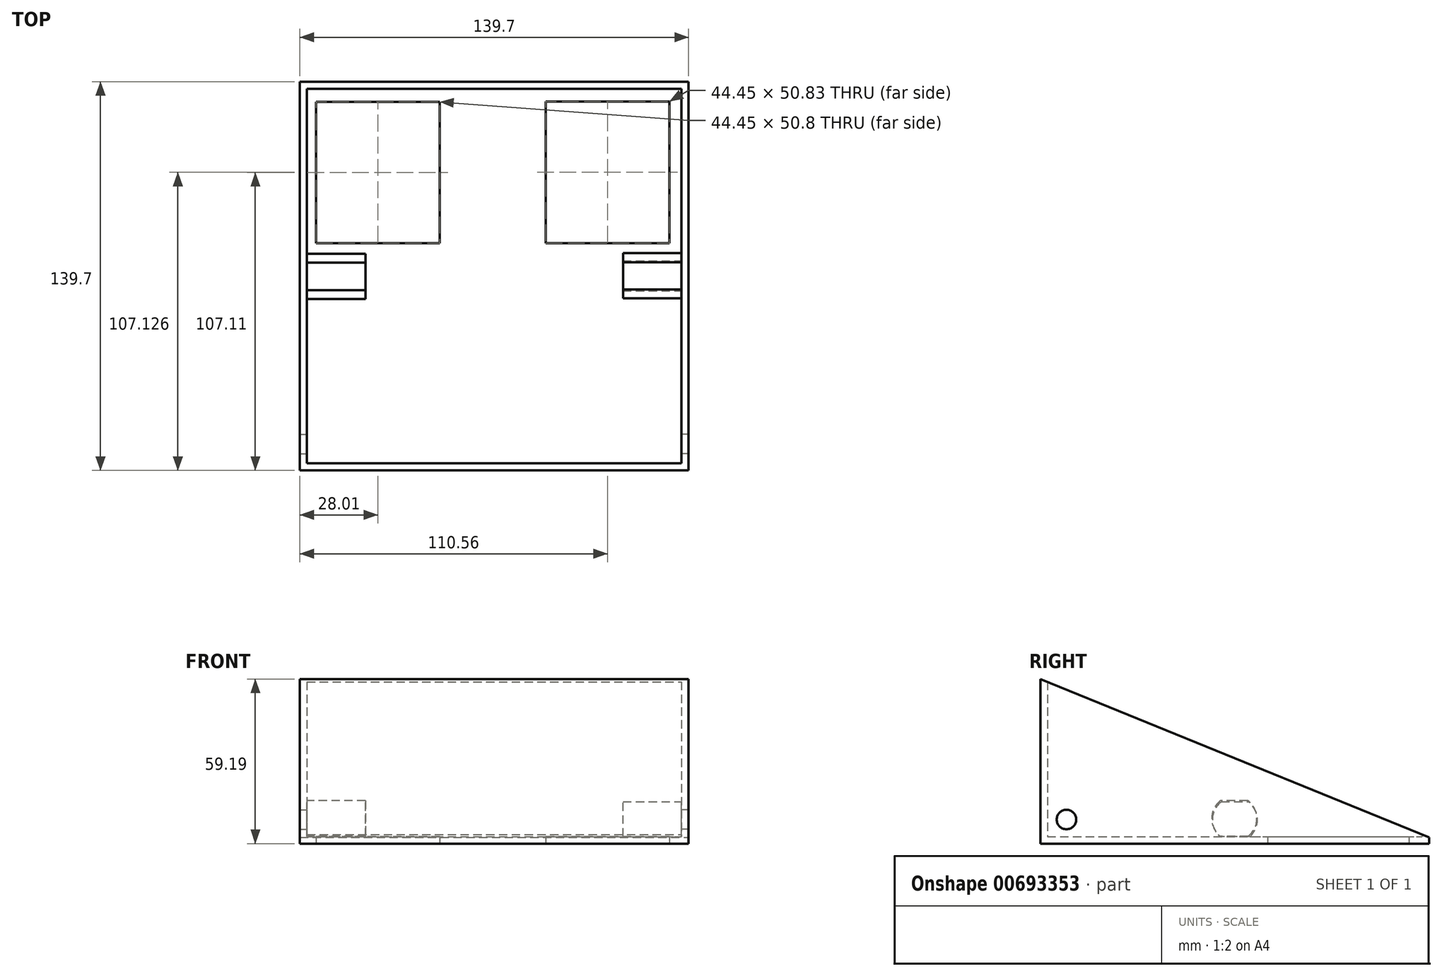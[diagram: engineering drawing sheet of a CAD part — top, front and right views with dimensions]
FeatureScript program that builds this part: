
annotation { "Feature Type Name" : "Feature", "Feature Type Description" : "" }
export const myFeature = defineFeature(function(context is Context, id is Id, definition is map)
    precondition{}
    {
        {
            var Q0;
            Q0=qCreatedBy(makeId("Front.planeOp"),FACE);
            var sketch = newSketch(context, id + "F0", { "sketchPlane" : qUnion([Q0])});
            skLineSegment(sketch, "E0.bottom", {"start": v(-62.53, 207.24) * mm, "end": v(77.17, 207.24) * mm});
            skLineSegment(sketch, "E0.top", {"start": v(-62.53, 67.54) * mm, "end": v(77.17, 67.54) * mm});
            skLineSegment(sketch, "E0.left", {"start": v(-62.53, 207.24) * mm, "end": v(-62.53, 67.54) * mm});
            skLineSegment(sketch, "E0.right", {"start": v(77.17, 207.24) * mm, "end": v(77.17, 67.54) * mm});
            skSolve(sketch);
        }
        {
            var Q0;
            Q0=qCreatedBy(makeId("Right.planeOp"),FACE);
            var sketch = newSketch(context, id + "F1", { "sketchPlane" : qUnion([Q0])});
            skCircle(sketch, "E1", {"center": v(-60.44, 76.2) * mm, "radius": 3.5 * mm});
            skSolve(sketch);
        }
        {
            var Q0;
            Q0 = qSketchRegion(id + "F0", true);
            extrude(context, id + "F2", {"entities" : qUnion([Q0]), "endBound" : BoundingType.SYMMETRIC, "depth" : 139.7 * mm, "offsetDistance" : 25.4 * mm});
        }
        {
            var Q0;
            Q0=qCreatedBy(makeId("Top.planeOp"),FACE);
            var sketch = newSketch(context, id + "F3", { "sketchPlane" : qUnion([Q0])});
            skLineSegment(sketch, "E2.bottom", {"start": v(-56.74, 62.66) * mm, "end": v(-12.3, 62.66) * mm});
            skLineSegment(sketch, "E2.top", {"start": v(-56.74, 62.66) * mm, "end": v(-12.3, 62.66) * mm});
            skLineSegment(sketch, "E2.left", {"start": v(-56.74, 62.66) * mm, "end": v(-56.74, 62.66) * mm});
            skLineSegment(sketch, "E2.right", {"start": v(-12.3, 62.66) * mm, "end": v(-12.3, 62.66) * mm});
            skLineSegment(sketch, "E3.top", {"start": v(-56.74, 11.86) * mm, "end": v(-12.3, 11.86) * mm});
            skLineSegment(sketch, "E3.left", {"start": v(-56.74, 62.66) * mm, "end": v(-56.74, 11.86) * mm});
            skLineSegment(sketch, "E3.right", {"start": v(-12.3, 62.66) * mm, "end": v(-12.3, 11.86) * mm});
            skLineSegment(sketch, "E4.bottom", {"start": v(25.8, 62.7) * mm, "end": v(70.26, 62.7) * mm});
            skLineSegment(sketch, "E4.top", {"start": v(25.8, 11.86) * mm, "end": v(70.26, 11.86) * mm});
            skLineSegment(sketch, "E4.left", {"start": v(25.8, 62.7) * mm, "end": v(25.8, 11.86) * mm});
            skLineSegment(sketch, "E4.right", {"start": v(70.26, 62.7) * mm, "end": v(70.26, 11.86) * mm});
            skSolve(sketch);
        }
        {
            var Q0;
            Q0 = qSketchRegion(id + "F3", true);
            extrude(context, id + "F4", {"entities" : qUnion([Q0]), "endBound" : BoundingType.SYMMETRIC, "depth" : 203.2 * mm, "offsetDistance" : 25.4 * mm});
        }
        {
            var Q0;
            Q0=qCreatedBy(makeId("Right.planeOp"),FACE);
            var sketch = newSketch(context, id + "F5", { "sketchPlane" : qUnion([Q0])});
            skLineSegment(sketch, "E5.bottom", {"start": v(134.32, 208.08) * mm, "end": v(-53.85, 284.79) * mm});
            skLineSegment(sketch, "E5.top", {"start": v(76.79, 66.96) * mm, "end": v(-111.38, 143.66) * mm});
            skLineSegment(sketch, "E5.left", {"start": v(134.32, 208.08) * mm, "end": v(76.79, 66.96) * mm});
            skLineSegment(sketch, "E5.right", {"start": v(-53.85, 284.79) * mm, "end": v(-111.38, 143.66) * mm});
            skSolve(sketch);
        }
        {
            var Q0;
            Q0 = qSketchRegion(id + "F5", true);
            extrude(context, id + "F6", {"entities" : qUnion([Q0]), "endBound" : BoundingType.SYMMETRIC, "depth" : 203.2 * mm, "offsetDistance" : 25.4 * mm});
        }
        {
            var Q0;
            Q0=makeQuery(id+"F6.opExtrude","SWEPT_BODY",BODY,{"disambiguationData":[OSD([sQuery(id+"F5.wireOp",EDGE,"E5.bottom"),sQuery(id+"F5.wireOp",EDGE,"E5.top"),sQuery(id+"F5.wireOp",EDGE,"E5.left"),sQuery(id+"F5.wireOp",EDGE,"E5.right")])]});
            var Q1;
            Q1=makeQuery(id+"F2.opExtrude","SWEPT_BODY",BODY,{"disambiguationData":[OSD([sQuery(id+"F0.wireOp",EDGE,"E0.bottom"),sQuery(id+"F0.wireOp",EDGE,"E0.top"),sQuery(id+"F0.wireOp",EDGE,"E0.left"),sQuery(id+"F0.wireOp",EDGE,"E0.right")])]});
            booleanBodies(context, id + "F7", {"operationType" : BooleanOperationType.SUBTRACTION, "tools" : qUnion([Q0]), "targets" : qUnion([Q1])});
        }
        {
            var Q0;
            Q0=makeQuery(id+"F7.opBoolean","COPY",FACE,{"derivedFrom":makeQuery(id+"F6.opExtrude","SWEPT_FACE",FACE,{"disambiguationData":[OSD([sQuery(id+"F5.wireOp",EDGE,"E5.top")])]})});
            shell(context, id + "F8", {"entities" : qUnion([Q0]), "thickness" : 2.54 * mm});
        }
        {
            var Q0;
            Q0=makeQuery(id+"F4.opExtrude","SWEPT_BODY",BODY,{"disambiguationData":[OSD([sQuery(id+"F3.wireOp",EDGE,"E4.bottom"),sQuery(id+"F3.wireOp",EDGE,"E4.top"),sQuery(id+"F3.wireOp",EDGE,"E4.left"),sQuery(id+"F3.wireOp",EDGE,"E4.right")])]});
            var Q1;
            Q1=makeQuery(id+"F4.opExtrude","SWEPT_BODY",BODY,{"disambiguationData":[OSD([sQuery(id+"F3.wireOp",EDGE,"E2.bottom"),sQuery(id+"F3.wireOp",EDGE,"E3.top"),sQuery(id+"F3.wireOp",EDGE,"E3.left"),sQuery(id+"F3.wireOp",EDGE,"E3.right")])]});
            var Q2;
            Q2=makeQuery(id+"F2.opExtrude","SWEPT_BODY",BODY,{"disambiguationData":[OSD([sQuery(id+"F0.wireOp",EDGE,"E0.bottom"),sQuery(id+"F0.wireOp",EDGE,"E0.top"),sQuery(id+"F0.wireOp",EDGE,"E0.left"),sQuery(id+"F0.wireOp",EDGE,"E0.right")])]});
            booleanBodies(context, id + "F9", {"operationType" : BooleanOperationType.SUBTRACTION, "tools" : qUnion([Q0, Q1]), "targets" : qUnion([Q2])});
        }
        {
            var Q0;
            Q0=sQuery(id+"F1.wireOp",VERTEX,"E1.center");
            var Q1;
            Q1=makeQuery(id+"F2.opExtrude","SWEPT_BODY",BODY,{"disambiguationData":[OSD([sQuery(id+"F0.wireOp",EDGE,"E0.bottom"),sQuery(id+"F0.wireOp",EDGE,"E0.top"),sQuery(id+"F0.wireOp",EDGE,"E0.left"),sQuery(id+"F0.wireOp",EDGE,"E0.right")])]});
            hole(context, id + "F10", {"style" : HoleStyle.SIMPLE, "endStyle" : HoleEndStyle.THROUGH, "holeDiameter" : 7 * mm, "majorDiameter" : 6.35 * mm, "isTappedThrough" : true, "tappedDepth" : 12.7 * mm, "tapClearance" : 3, "locations" : qUnion([Q0]), "scope" : qUnion([Q1])});
        }
        {
            var Q0;
            Q0=sQuery(id+"F1.wireOp",VERTEX,"E1.center");
            var Q1;
            Q1=makeQuery(id+"F2.opExtrude","SWEPT_BODY",BODY,{"disambiguationData":[OSD([sQuery(id+"F0.wireOp",EDGE,"E0.bottom"),sQuery(id+"F0.wireOp",EDGE,"E0.top"),sQuery(id+"F0.wireOp",EDGE,"E0.left"),sQuery(id+"F0.wireOp",EDGE,"E0.right")])]});
            hole(context, id + "F11", {"style" : HoleStyle.SIMPLE, "endStyle" : HoleEndStyle.THROUGH, "oppositeDirection" : true, "holeDiameter" : 7 * mm, "majorDiameter" : 6.35 * mm, "isTappedThrough" : true, "tappedDepth" : 12.7 * mm, "tapClearance" : 3, "locations" : qUnion([Q0]), "scope" : qUnion([Q1])});
        }
        {
            var Q0;
            Q0=makeQuery(id+"F8.opShell","OFFSET_FACE",FACE,{"disambiguationData":[OSD([sQuery(id+"F0.wireOp",EDGE,"E0.right")])]});
            var sketch = newSketch(context, id + "F12", { "sketchPlane" : qUnion([Q0])});
            skArc(sketch, "E6", {"start": v(-5, 82.55) * mm, "mid": v(-8.2, 76.1) * mm, "end": v(-5, 69.65) * mm});
            skArc(sketch, "E7.trimOffspring", {"start": v(4.83, 69.68) * mm, "mid": v(8, 76.12) * mm, "end": v(4.8, 82.55) * mm});
            skLineSegment(sketch, "E8.trimOffspring", {"start": v(4.83, 69.68) * mm, "end": v(-5, 69.65) * mm});
            skLineSegment(sketch, "E9.trimOffspring", {"start": v(4.8, 82.55) * mm, "end": v(-5, 82.55) * mm});
            skSolve(sketch);
        }
        {
            var Q0;
            Q0 = qSketchRegion(id + "F12", true);
            extrude(context, id + "F13", {"entities" : qUnion([Q0]), "operationType" : NewBodyOperationType.ADD, "depth" : 21 * mm, "offsetDistance" : 25.4 * mm});
        }
        {
            var Q0;
            Q0=makeQuery(id+"F8.opShell","OFFSET_FACE",FACE,{"disambiguationData":[OSD([sQuery(id+"F0.wireOp",EDGE,"E0.left")])]});
            var sketch = newSketch(context, id + "F14", { "sketchPlane" : qUnion([Q0])});
            skArc(sketch, "E10", {"start": v(-5.03, 83) * mm, "mid": v(-8.23, 76.55) * mm, "end": v(-5.03, 70.1) * mm});
            skArc(sketch, "E11.trimOffspring", {"start": v(4.8, 70.12) * mm, "mid": v(7.97, 76.56) * mm, "end": v(4.77, 83) * mm});
            skLineSegment(sketch, "E12.trimOffspring", {"start": v(4.8, 70.12) * mm, "end": v(-5.03, 70.1) * mm});
            skLineSegment(sketch, "E13.trimOffspring", {"start": v(4.77, 83) * mm, "end": v(-5.03, 83) * mm});
            skSolve(sketch);
        }
        {
            var Q0;
            Q0 = qSketchRegion(id + "F14", true);
            extrude(context, id + "F15", {"entities" : qUnion([Q0]), "operationType" : NewBodyOperationType.ADD, "depth" : 21 * mm, "offsetDistance" : 25.4 * mm});
        }
    });
